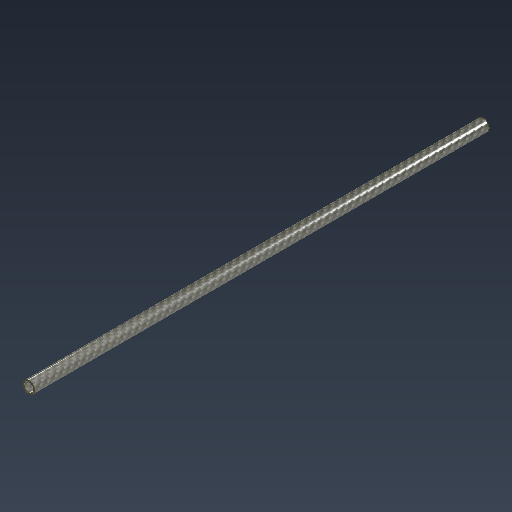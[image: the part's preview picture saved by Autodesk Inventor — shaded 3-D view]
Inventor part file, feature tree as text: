
AUTODESK INVENTOR PART (.ipt)
format: ipt  version: 2025 (Build 290162010, 162A)  size: 113,152 bytes
history: native  units: mm
features: extrude x1
ambient origin geometry x8: Origin, YZ Plane, XZ Plane, XY Plane, X Axis, Y Axis, Z Axis, Center Point
bodies: Solid1 (feature_tree)
feature tree (1):
  extrude  "Extrusion1"  Depth=12.0mm
